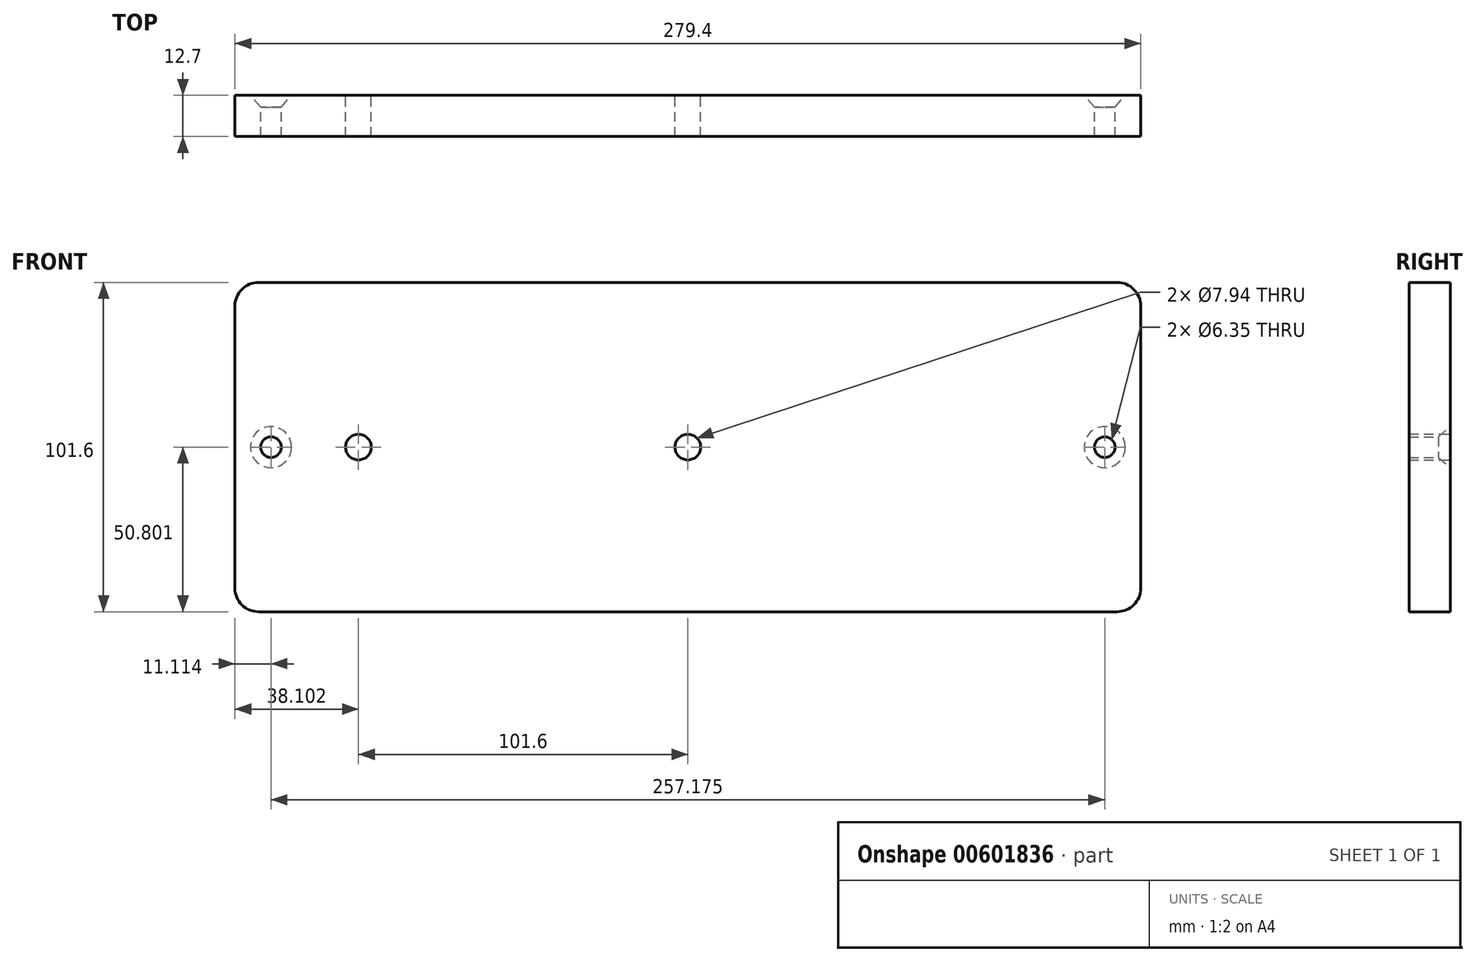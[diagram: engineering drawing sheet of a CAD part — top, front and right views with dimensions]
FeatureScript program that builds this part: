
annotation { "Feature Type Name" : "Feature", "Feature Type Description" : "" }
export const myFeature = defineFeature(function(context is Context, id is Id, definition is map)
    precondition{}
    {
        {
            var Q0;
            Q0=qCreatedBy(makeId("Front.planeOp"),FACE);
            var sketch = newSketch(context, id + "F0", { "sketchPlane" : qUnion([Q0])});
            skLineSegment(sketch, "E0.bottom", {"start": v(-136.62, 9.64) * mm, "end": v(142.78, 9.64) * mm});
            skLineSegment(sketch, "E0.top", {"start": v(-136.62, -91.96) * mm, "end": v(142.78, -91.96) * mm});
            skLineSegment(sketch, "E0.left", {"start": v(-136.62, 9.64) * mm, "end": v(-136.62, -91.96) * mm});
            skLineSegment(sketch, "E0.right", {"start": v(142.78, 9.64) * mm, "end": v(142.78, -91.96) * mm});
            skLineSegment(sketch, "E1", {"start": v(-136.62, -41.16) * mm, "end": v(142.78, -41.16) * mm, "construction": true});
            skLineSegment(sketch, "E2", {"start": v(-125.5, 9.64) * mm, "end": v(-125.5, -91.96) * mm, "construction": true});
            skLineSegment(sketch, "E3", {"start": v(-98.52, 9.64) * mm, "end": v(-98.52, -91.96) * mm, "construction": true});
            skLineSegment(sketch, "E4", {"start": v(3.08, 9.64) * mm, "end": v(3.08, -91.96) * mm, "construction": true});
            skLineSegment(sketch, "E5", {"start": v(131.67, 9.64) * mm, "end": v(131.67, -91.96) * mm, "construction": true});
            skPoint(sketch, "E6", {"position": v(-125.5, -41.16) * mm});
            skPoint(sketch, "E7", {"position": v(-98.52, -41.16) * mm});
            skPoint(sketch, "E8", {"position": v(3.08, -41.16) * mm});
            skPoint(sketch, "E9", {"position": v(131.67, -41.16) * mm});
            skSolve(sketch);
        }
        {
            var Q0;
            Q0 = qSketchRegion(id + "F0", true);
            extrude(context, id + "F1", {"entities" : qUnion([Q0]), "depth" : 12.7 * mm, "offsetDistance" : 25.4 * mm});
        }
        {
            var Q0;
            Q0=sQuery(id+"F0.wireOp",VERTEX,"E7");
            var Q1;
            Q1=sQuery(id+"F0.wireOp",VERTEX,"E8");
            var Q2;
            Q2=makeQuery(id+"F1.opExtrude","SWEPT_BODY",BODY,{"disambiguationData":[OSD([sQuery(id+"F0.wireOp",EDGE,"E0.bottom"),sQuery(id+"F0.wireOp",EDGE,"E0.top"),sQuery(id+"F0.wireOp",EDGE,"E0.left"),sQuery(id+"F0.wireOp",EDGE,"E0.right")])]});
            hole(context, id + "F2", {"style" : HoleStyle.SIMPLE, "endStyle" : HoleEndStyle.THROUGH, "oppositeDirection" : true, "holeDiameter" : 7.94 * mm, "majorDiameter" : 6.35 * mm, "isTappedThrough" : true, "tappedDepth" : 12.7 * mm, "tapClearance" : 3, "locations" : qUnion([Q0, Q1]), "scope" : qUnion([Q2])});
        }
        {
            var Q0;
            Q0=sQuery(id+"F0.wireOp",VERTEX,"E6");
            var Q1;
            Q1=sQuery(id+"F0.wireOp",VERTEX,"E9");
            var Q2;
            Q2=makeQuery(id+"F1.opExtrude","SWEPT_BODY",BODY,{"disambiguationData":[OSD([sQuery(id+"F0.wireOp",EDGE,"E0.bottom"),sQuery(id+"F0.wireOp",EDGE,"E0.top"),sQuery(id+"F0.wireOp",EDGE,"E0.left"),sQuery(id+"F0.wireOp",EDGE,"E0.right")])]});
            hole(context, id + "F3", {"style" : HoleStyle.C_SINK, "endStyle" : HoleEndStyle.THROUGH, "oppositeDirection" : true, "holeDiameter" : 6.35 * mm, "cSinkDiameter" : 12.7 * mm, "cSinkAngle" : 82 * degree, "majorDiameter" : 6.35 * mm, "isTappedThrough" : true, "tappedDepth" : 12.7 * mm, "tapClearance" : 3, "locations" : qUnion([Q0, Q1]), "scope" : qUnion([Q2])});
        }
        {
            var Q0;
            Q0=makeQuery(id+"F1.opExtrude","SWEPT_EDGE",EDGE,{"disambiguationData":[OSD([sQuery(id+"F0.wireOp",EDGE,"E0.bottom"),sQuery(id+"F0.wireOp",EDGE,"E0.right")])]});
            var Q1;
            Q1=makeQuery(id+"F1.opExtrude","SWEPT_EDGE",EDGE,{"disambiguationData":[OSD([sQuery(id+"F0.wireOp",EDGE,"E0.bottom"),sQuery(id+"F0.wireOp",EDGE,"E0.left")])]});
            var Q2;
            Q2=makeQuery(id+"F1.opExtrude","SWEPT_EDGE",EDGE,{"disambiguationData":[OSD([sQuery(id+"F0.wireOp",EDGE,"E0.top"),sQuery(id+"F0.wireOp",EDGE,"E0.left")])]});
            var Q3;
            Q3=makeQuery(id+"F1.opExtrude","SWEPT_EDGE",EDGE,{"disambiguationData":[OSD([sQuery(id+"F0.wireOp",EDGE,"E0.top"),sQuery(id+"F0.wireOp",EDGE,"E0.right")])]});
            fillet(context, id + "F4", {"entities" : qUnion([Q0, Q1, Q2, Q3]), "radius" : 7.3 * mm, "tangentPropagation" : true, "allowEdgeOverflow" : false});
        }
    });
